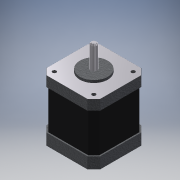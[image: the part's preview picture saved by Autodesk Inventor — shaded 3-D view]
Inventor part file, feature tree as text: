
AUTODESK INVENTOR PART (.ipt)
format: ipt  version: 2016 SP1 (Build 200210100, 210)  size: 424,960 bytes
history: native  units: mm
features: sketch x19, other x3, plane x1
ambient origin geometry x8: Origin, YZ Plane, XZ Plane, XY Plane, X Axis, Y Axis, Z Axis, Center Point
bodies: Solid1 (feature_tree)
feature tree (23):
  other  "NEMA17 Stepper.ipt"
  other  "Solid1::NEMA17 Stepper.ipt"
  other  "TaggingFeature1"
  sketch  "Sketch1"  dims[d0=10.0mm]
  sketch  "Sketch2"
  sketch  "Sketch3"
  sketch  "Sketch4"
  sketch  "Sketch5"
  sketch  "Sketch7"
  sketch  "Sketch8"
  sketch  "Sketch9"
  sketch  "Sketch10"
  sketch  "Sketch11"
  sketch  "Sketch12"
  sketch  "Sketch13"
  sketch  "Sketch14"
  sketch  "Sketch15"
  sketch  "Sketch16"
  sketch  "Sketch17"
  sketch  "Sketch18"
  sketch  "Sketch19"
  sketch  "Sketch20"
  plane  "Work Plane1"
